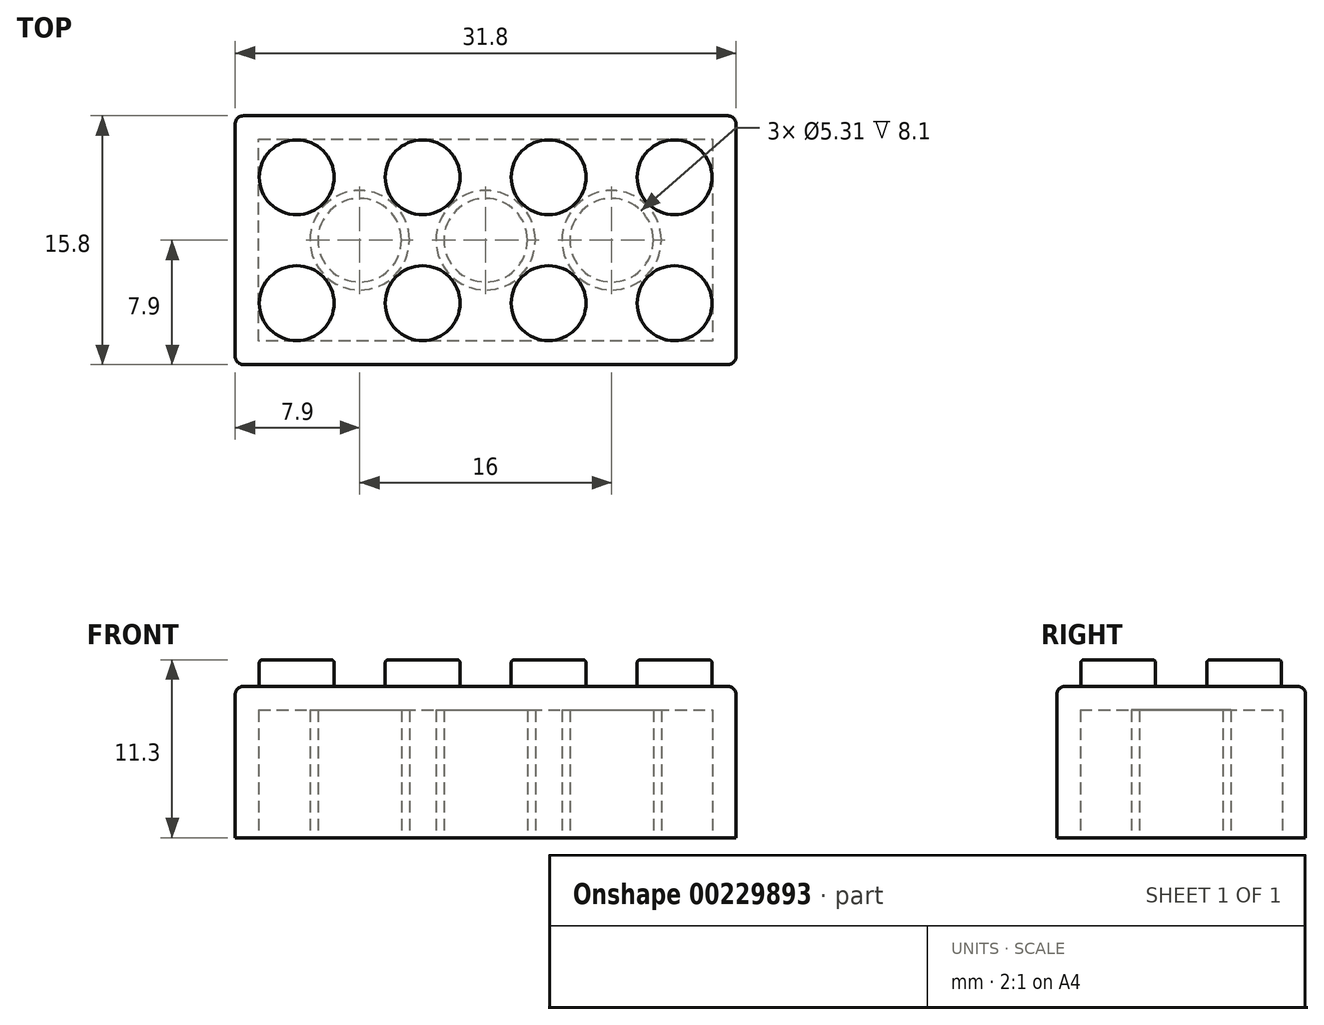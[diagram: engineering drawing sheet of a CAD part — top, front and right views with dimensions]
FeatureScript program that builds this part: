
annotation { "Feature Type Name" : "Feature", "Feature Type Description" : "" }
export const myFeature = defineFeature(function(context is Context, id is Id, definition is map)
    precondition{}
    {
        {
            var Q0;
            Q0=qCreatedBy(makeId("Top.planeOp"),FACE);
            var sketch = newSketch(context, id + "F0", { "sketchPlane" : qUnion([Q0])});
            skLineSegment(sketch, "E0.bottom", {"start": v(0.5, 0) * mm, "end": v(31.3, 0) * mm});
            skLineSegment(sketch, "E0.top", {"start": v(0.5, 15.8) * mm, "end": v(31.3, 15.8) * mm});
            skLineSegment(sketch, "E0.left", {"start": v(0, 0.5) * mm, "end": v(0, 15.3) * mm});
            skLineSegment(sketch, "E0.right", {"start": v(31.8, 0.5) * mm, "end": v(31.8, 15.3) * mm});
            skPoint(sketch, "E1.visualSharp", {"position": v(0, 15.8) * mm});
            skArc(sketch, "E1.filletArc", {"start": v(0.5, 15.8) * mm, "mid": v(0.15, 15.65) * mm, "end": v(0, 15.3) * mm});
            skPoint(sketch, "E2.visualSharp", {"position": v(31.8, 15.8) * mm});
            skArc(sketch, "E2.filletArc", {"start": v(31.8, 15.3) * mm, "mid": v(31.65, 15.65) * mm, "end": v(31.3, 15.8) * mm});
            skPoint(sketch, "E3.visualSharp", {"position": v(31.8, 0) * mm});
            skArc(sketch, "E3.filletArc", {"start": v(31.3, 0) * mm, "mid": v(31.65, 0.15) * mm, "end": v(31.8, 0.5) * mm});
            skPoint(sketch, "E4.visualSharp", {"position": v(0, 0) * mm});
            skArc(sketch, "E4.filletArc", {"start": v(0, 0.5) * mm, "mid": v(0.15, 0.15) * mm, "end": v(0.5, 0) * mm});
            skSolve(sketch);
        }
        {
            var Q0;
            Q0 = qSketchRegion(id + "F0", true);
            extrude(context, id + "F1", {"entities" : qUnion([Q0]), "depth" : 9.6 * mm});
        }
        {
            var Q0;
            Q0=makeQuery(id+"F1.opExtrude","CAP_EDGE",EDGE,{"disambiguationData":[OSD([sQuery(id+"F0.wireOp",EDGE,"E0.bottom")])],"isStart":false});
            fillet(context, id + "F2", {"entities" : qUnion([Q0]), "radius" : 0.5 * mm, "tangentPropagation" : true, "allowEdgeOverflow" : false});
        }
        {
            var Q0;
            Q0=makeQuery(id+"F1.opExtrude","CAP_FACE",FACE,{"disambiguationData":[OSD([sQuery(id+"F0.wireOp",EDGE,"E0.bottom"),sQuery(id+"F0.wireOp",EDGE,"E0.top"),sQuery(id+"F0.wireOp",EDGE,"E0.left"),sQuery(id+"F0.wireOp",EDGE,"E0.right"),sQuery(id+"F0.wireOp",EDGE,"E1.filletArc"),sQuery(id+"F0.wireOp",EDGE,"E2.filletArc"),sQuery(id+"F0.wireOp",EDGE,"E3.filletArc"),sQuery(id+"F0.wireOp",EDGE,"E4.filletArc")])],"isStart":false});
            var sketch = newSketch(context, id + "F3", { "sketchPlane" : qUnion([Q0])});
            skCircle(sketch, "E5", {"center": v(3.9, 3.9) * mm, "radius": 2.38 * mm});
            skCircle(sketch, "E6.0.1.0", {"center": v(3.9, 11.9) * mm, "radius": 2.38 * mm});
            skCircle(sketch, "E6.1.0.0", {"center": v(11.9, 3.9) * mm, "radius": 2.38 * mm});
            skCircle(sketch, "E6.1.1.0", {"center": v(11.9, 11.9) * mm, "radius": 2.38 * mm});
            skCircle(sketch, "E6.2.0.0", {"center": v(19.9, 3.9) * mm, "radius": 2.38 * mm});
            skCircle(sketch, "E6.2.1.0", {"center": v(19.9, 11.9) * mm, "radius": 2.38 * mm});
            skCircle(sketch, "E6.3.0.0", {"center": v(27.9, 3.9) * mm, "radius": 2.38 * mm});
            skCircle(sketch, "E6.3.1.0", {"center": v(27.9, 11.9) * mm, "radius": 2.38 * mm});
            skLineSegment(sketch, "E6.direction1", {"start": v(3.9, 3.9) * mm, "end": v(11.9, 3.9) * mm, "construction": true});
            skLineSegment(sketch, "E6.direction2", {"start": v(3.9, 3.9) * mm, "end": v(3.9, 11.9) * mm, "construction": true});
            skSolve(sketch);
        }
        {
            var Q0;
            Q0 = qSketchRegion(id + "F3", true);
            extrude(context, id + "F4", {"entities" : qUnion([Q0]), "operationType" : NewBodyOperationType.ADD, "depth" : 1.7 * mm});
        }
        {
            var Q0;
            Q0=makeQuery(id+"F4.opExtrude","CAP_EDGE",EDGE,{"disambiguationData":[OSD([sQuery(id+"F3.wireOp",EDGE,"E5")])],"isStart":false});
            var Q1;
            Q1=makeQuery(id+"F4.opExtrude","CAP_EDGE",EDGE,{"disambiguationData":[OSD([sQuery(id+"F3.wireOp",EDGE,"E6.0.1.0")])],"isStart":false});
            var Q2;
            Q2=makeQuery(id+"F4.opExtrude","CAP_EDGE",EDGE,{"disambiguationData":[OSD([sQuery(id+"F3.wireOp",EDGE,"E6.1.1.0")])],"isStart":false});
            var Q3;
            Q3=makeQuery(id+"F4.opExtrude","CAP_EDGE",EDGE,{"disambiguationData":[OSD([sQuery(id+"F3.wireOp",EDGE,"E6.1.0.0")])],"isStart":false});
            var Q4;
            Q4=makeQuery(id+"F4.opExtrude","CAP_EDGE",EDGE,{"disambiguationData":[OSD([sQuery(id+"F3.wireOp",EDGE,"E6.2.0.0")])],"isStart":false});
            var Q5;
            Q5=makeQuery(id+"F4.opExtrude","CAP_EDGE",EDGE,{"disambiguationData":[OSD([sQuery(id+"F3.wireOp",EDGE,"E6.2.1.0")])],"isStart":false});
            var Q6;
            Q6=makeQuery(id+"F4.opExtrude","CAP_EDGE",EDGE,{"disambiguationData":[OSD([sQuery(id+"F3.wireOp",EDGE,"E6.3.1.0")])],"isStart":false});
            var Q7;
            Q7=makeQuery(id+"F4.opExtrude","CAP_EDGE",EDGE,{"disambiguationData":[OSD([sQuery(id+"F3.wireOp",EDGE,"E6.3.0.0")])],"isStart":false});
            fillet(context, id + "F5", {"entities" : qUnion([Q0, Q1, Q2, Q3, Q4, Q5, Q6, Q7]), "radius" : 0.2 * mm, "tangentPropagation" : true, "allowEdgeOverflow" : false});
        }
        {
            var Q0;
            Q0=makeQuery(id+"F1.opExtrude","CAP_FACE",FACE,{"disambiguationData":[OSD([sQuery(id+"F0.wireOp",EDGE,"E0.bottom"),sQuery(id+"F0.wireOp",EDGE,"E0.top"),sQuery(id+"F0.wireOp",EDGE,"E0.left"),sQuery(id+"F0.wireOp",EDGE,"E0.right"),sQuery(id+"F0.wireOp",EDGE,"E1.filletArc"),sQuery(id+"F0.wireOp",EDGE,"E2.filletArc"),sQuery(id+"F0.wireOp",EDGE,"E3.filletArc"),sQuery(id+"F0.wireOp",EDGE,"E4.filletArc")])],"isStart":true});
            var sketch = newSketch(context, id + "F6", { "sketchPlane" : qUnion([Q0])});
            skLineSegment(sketch, "E7.0", {"start": v(1.49, -14.31) * mm, "end": v(30.31, -14.31) * mm});
            skLineSegment(sketch, "E7.1", {"start": v(1.49, -1.49) * mm, "end": v(1.49, -14.31) * mm});
            skLineSegment(sketch, "E7.2", {"start": v(30.31, -1.49) * mm, "end": v(1.49, -1.49) * mm});
            skLineSegment(sketch, "E7.3", {"start": v(30.31, -14.31) * mm, "end": v(30.31, -1.49) * mm});
            skCircle(sketch, "E8", {"center": v(7.9, -7.9) * mm, "radius": 3.15 * mm});
            skLineSegment(sketch, "E9", {"start": v(0, -7.9) * mm, "end": v(31.8, -7.9) * mm, "construction": true});
            skCircle(sketch, "E10", {"center": v(7.9, -7.9) * mm, "radius": 2.65 * mm});
            skCircle(sketch, "E11.1.0.0", {"center": v(15.9, -7.9) * mm, "radius": 2.65 * mm});
            skCircle(sketch, "E11.1.0.1", {"center": v(15.9, -7.9) * mm, "radius": 3.15 * mm});
            skCircle(sketch, "E11.2.0.0", {"center": v(23.9, -7.9) * mm, "radius": 2.65 * mm});
            skCircle(sketch, "E11.2.0.1", {"center": v(23.9, -7.9) * mm, "radius": 3.15 * mm});
            skLineSegment(sketch, "E11.direction1", {"start": v(7.9, -7.9) * mm, "end": v(15.9, -7.9) * mm, "construction": true});
            skSolve(sketch);
        }
        {
            var Q0;
            Q0=makeQuery(id+"F6.imprint","IMPRINT",FACE,{"disambiguationData":[TD([[makeQuery(id+"F6.imprint","IMPRINT",EDGE,{"derivedFrom":sQuery(id+"F6.wireOp",EDGE,"E7.0")}),1.0]])]});
            var Q1;
            Q1=makeQuery(id+"F6.imprint","IMPRINT",FACE,{"disambiguationData":[TD([[makeQuery(id+"F6.imprint","IMPRINT",EDGE,{"derivedFrom":sQuery(id+"F6.wireOp",EDGE,"E10")}),1.0]])]});
            var Q2;
            Q2=makeQuery(id+"F6.imprint","IMPRINT",FACE,{"disambiguationData":[TD([[makeQuery(id+"F6.imprint","IMPRINT",EDGE,{"derivedFrom":sQuery(id+"F6.wireOp",EDGE,"E11.1.0.0")}),1.0]])]});
            var Q3;
            Q3=makeQuery(id+"F6.imprint","IMPRINT",FACE,{"disambiguationData":[TD([[makeQuery(id+"F6.imprint","IMPRINT",EDGE,{"derivedFrom":sQuery(id+"F6.wireOp",EDGE,"E11.2.0.0")}),1.0]])]});
            extrude(context, id + "F7", {"entities" : qUnion([Q0, Q1, Q2, Q3]), "operationType" : NewBodyOperationType.REMOVE, "oppositeDirection" : true, "depth" : 8.1 * mm});
        }
    });
